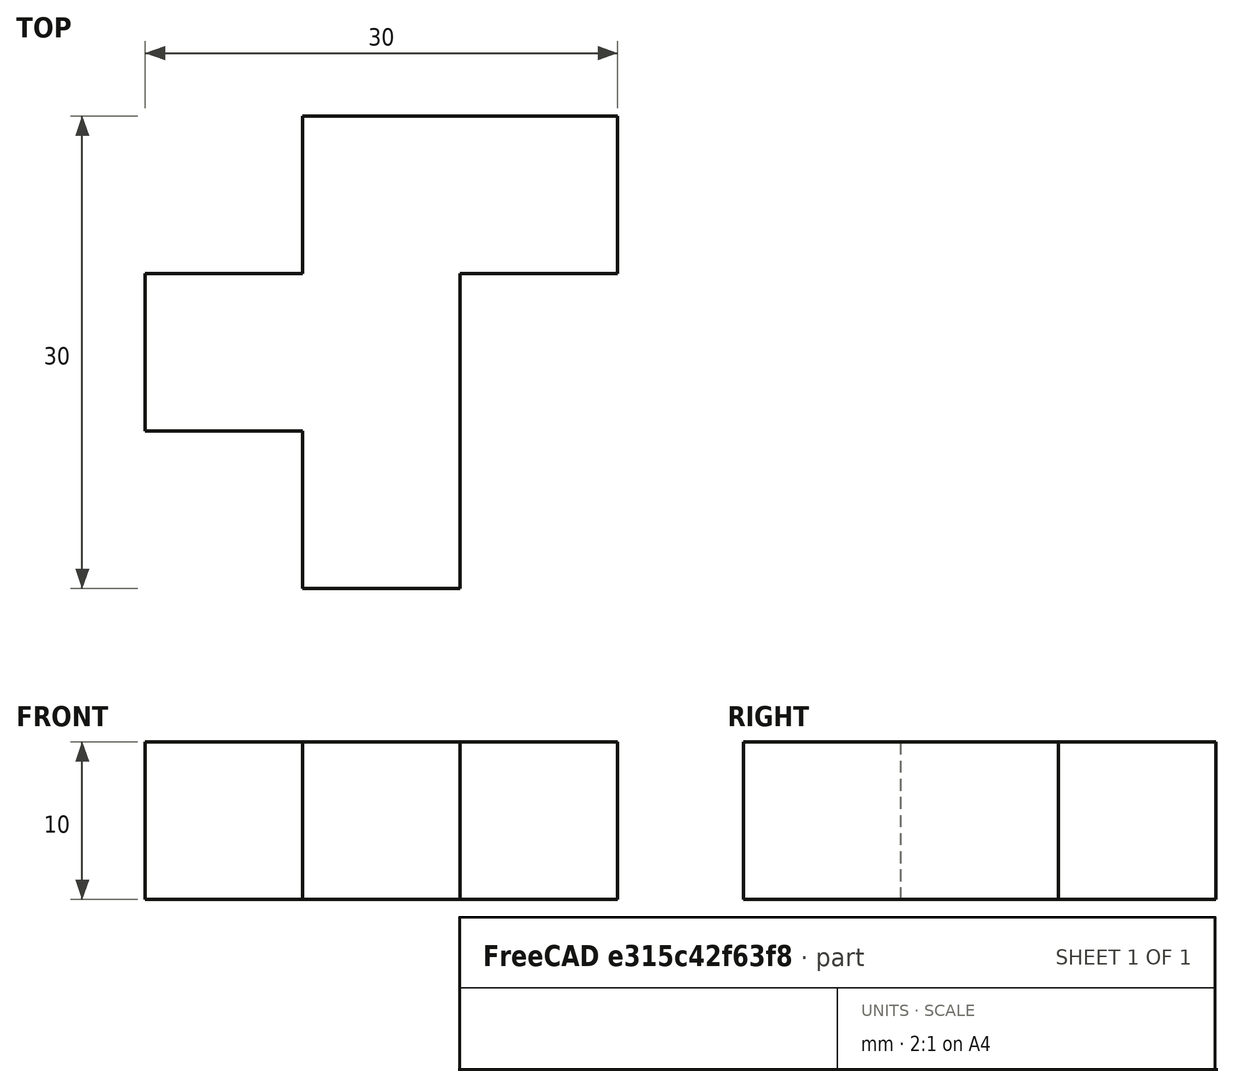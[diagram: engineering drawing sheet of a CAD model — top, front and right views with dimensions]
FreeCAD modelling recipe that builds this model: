
FCSTD DOCUMENT  (FreeCAD 0.16R)
Label: F
License: All rights reserved
LicenseURL: http://en.wikipedia.org/wiki/All_rights_reserved
objects: Sketcher::SketchObject×1, PartDesign::Pad×1
note: 3 computed .brp shape members not serialized (recipe doc carries the construction recipe); baked Part::Feature solids carry a one-line shape summary decoded from their .brp

FEATURE [Sketcher::SketchObject] Sketch
  sketch-geometry (10):
    g0: LineSegment StartX=-10 StartY=30 StartZ=0 EndX=-10 EndY=20 EndZ=0
    g1: LineSegment StartX=-10 StartY=20 StartZ=0 EndX=-20 EndY=20 EndZ=0
    g2: LineSegment StartX=-20 StartY=20 StartZ=0 EndX=-20 EndY=10 EndZ=0
    g3: LineSegment StartX=-20 StartY=10 StartZ=0 EndX=-10 EndY=10 EndZ=0
    g4: LineSegment StartX=-10 StartY=10 StartZ=0 EndX=-10 EndY=0 EndZ=0
    g5: LineSegment StartX=-10 StartY=0 StartZ=0 EndX=0 EndY=0 EndZ=0
    g6: LineSegment StartX=0 StartY=0 StartZ=0 EndX=0 EndY=20 EndZ=0
    g7: LineSegment StartX=0 StartY=20 StartZ=0 EndX=10 EndY=20 EndZ=0
    g8: LineSegment StartX=10 StartY=20 StartZ=0 EndX=10 EndY=30 EndZ=0
    g9: LineSegment StartX=10 StartY=30 StartZ=0 EndX=-10 EndY=30 EndZ=0
  constraints (29):
    c: Vertical(g0)
    c: Coincident(g0,g1)
    c: Horizontal(g1)
    c: Coincident(g1,g2)
    c: Coincident(g2,g3)
    c: Horizontal(g3)
    c: Coincident(g3,g4)
    c: Vertical(g4)
    c: Coincident(g4,g5)
    c: Horizontal(g5)
    c: Coincident(g5,g6)
    c: Coincident(g6,g7)
    c: Horizontal(g7)
    c: Coincident(g7,g8)
    c: Coincident(g8,g9)
    c: Coincident(g9,g0)
    c: Distance(g0) = 10
    c: Distance(g9) = 20
    c: Distance(g8) = 10
    c: Horizontal(g9)
    c: Vertical(g8)
    c: Vertical(g6)
    c: Distance(g7) = 10
    c: Distance(g6) = 20
    c: Distance(g4) = 10
    c: Distance(g1) = 10
    c: Distance(g2) = 10
    c: Distance(g3) = 10
    c: Coincident(g5,g-1)
FEATURE [PartDesign::Pad] Pad
  Length = 10
  Length2 = 100
  Sketch = -> Sketch
  Type = 0
